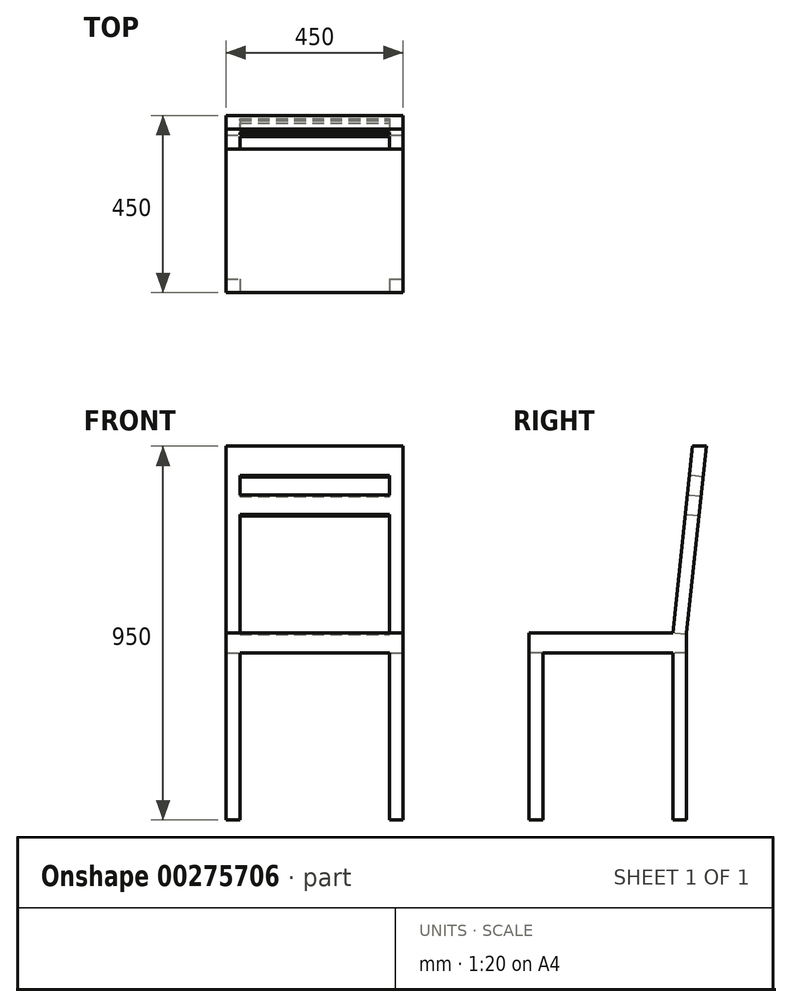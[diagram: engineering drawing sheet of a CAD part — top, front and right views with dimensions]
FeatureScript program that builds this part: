
annotation { "Feature Type Name" : "Feature", "Feature Type Description" : "" }
export const myFeature = defineFeature(function(context is Context, id is Id, definition is map)
    precondition{}
    {
        {
            var Q0;
            Q0=qCreatedBy(makeId("Top.planeOp"),FACE);
            var sketch = newSketch(context, id + "F0", { "sketchPlane" : qUnion([Q0])});
            skLineSegment(sketch, "E0.bottom", {"start": v(225, 225) * mm, "end": v(-225, 225) * mm});
            skLineSegment(sketch, "E0.top", {"start": v(225, -225) * mm, "end": v(-225, -225) * mm});
            skLineSegment(sketch, "E0.left", {"start": v(225, 225) * mm, "end": v(225, -225) * mm});
            skLineSegment(sketch, "E0.right", {"start": v(-225, 225) * mm, "end": v(-225, -225) * mm});
            skPoint(sketch, "E0.middle", {"position": v(0, 0) * mm});
            skSolve(sketch);
        }
        {
            var Q0;
            Q0=qSketchRegion(id+"F0",true);
            extrude(context, id + "F1", {"entities" : qUnion([Q0]), "depth" : 950 * mm});
        }
        {
            var Q0;
            Q0=makeQuery(id+"F1.opExtrude","SWEPT_FACE",FACE,{"disambiguationData":[OSD([sQuery(id+"F0.wireOp",EDGE,"E0.left")])]});
            var sketch = newSketch(context, id + "F2", { "sketchPlane" : qUnion([Q0])});
            skLineSegment(sketch, "E1.bottom", {"start": v(225, 475) * mm, "end": v(-225, 475) * mm});
            skLineSegment(sketch, "E1.top", {"start": v(225, 425) * mm, "end": v(-225, 425) * mm});
            skLineSegment(sketch, "E1.left", {"start": v(225, 475) * mm, "end": v(225, 425) * mm});
            skLineSegment(sketch, "E1.right", {"start": v(-225, 475) * mm, "end": v(-225, 425) * mm});
            skLineSegment(sketch, "E2", {"start": v(225, 950) * mm, "end": v(175, 475) * mm});
            skLineSegment(sketch, "E3", {"start": v(190, 950) * mm, "end": v(140, 475) * mm});
            skLineSegment(sketch, "E4", {"start": v(140, 475) * mm, "end": v(140, 0) * mm});
            skLineSegment(sketch, "E5", {"start": v(175, 475) * mm, "end": v(175, 0) * mm});
            skLineSegment(sketch, "E6.bottom", {"start": v(-225, 0) * mm, "end": v(-190, 0) * mm});
            skLineSegment(sketch, "E6.top", {"start": v(-225, 425) * mm, "end": v(-190, 425) * mm});
            skLineSegment(sketch, "E6.left", {"start": v(-225, 0) * mm, "end": v(-225, 425) * mm});
            skLineSegment(sketch, "E6.right", {"start": v(-190, 0) * mm, "end": v(-190, 425) * mm});
            skLineSegment(sketch, "E7", {"start": v(-225, 950) * mm, "end": v(-225, 0) * mm});
            skSolve(sketch);
        }
        {
            var Q0;
            {var subQ0=sQuery(id+"F2.wireOp",EDGE,"E1.left");Q0=makeQuery(id+"F2.imprint","IMPRINT",FACE,{"disambiguationData":[TD([[makeQuery(id+"F2.imprint","IMPRINT",EDGE,{"derivedFrom":subQ0}),-1.0]])]});}
            var Q1;
            {var subQ4=sQuery(id+"F2.wireOp",EDGE,"E3");Q1=makeQuery(id+"F2.imprint","IMPRINT",FACE,{"disambiguationData":[TD([[makeQuery(id+"F2.imprint","IMPRINT",EDGE,{"derivedFrom":subQ4}),-1.0]])]});}
            var Q2;
            {var subQ4=sQuery(id+"F2.wireOp",EDGE,"E2");Q2=makeQuery(id+"F2.imprint","IMPRINT",FACE,{"disambiguationData":[TD([[makeQuery(id+"F2.imprint","IMPRINT",EDGE,{"derivedFrom":subQ4}),1.0]])]});}
            var Q3;
            {var subQ1=sQuery(id+"F0.wireOp",EDGE,"E0.left");var subQ4=sQuery(id+"F2.wireOp",EDGE,"E5");var subQ6=makeQuery(id+"F1.opExtrude","CAP_EDGE",EDGE,{"disambiguationData":[OSD([subQ1])],"isStart":true});var subQ7=makeQuery(id+"F2.imprint","INTERSECT",VERTEX,{"derivedFrom":[subQ6,subQ4]});Q3=makeQuery(id+"F2.imprint","IMPRINT",FACE,{"disambiguationData":[TD([[makeQuery(id+"F2.imprint","IMPRINT",EDGE,{"disambiguationData":[TD([[subQ7,1.0]])],"derivedFrom":subQ4}),1.0]])]});}
            var Q4;
            {var subQ0=sQuery(id+"F2.wireOp",EDGE,"E6.right");Q4=makeQuery(id+"F2.imprint","IMPRINT",FACE,{"disambiguationData":[TD([[makeQuery(id+"F2.imprint","IMPRINT",EDGE,{"derivedFrom":subQ0}),-1.0]])]});}
            extrude(context, id + "F3", {"entities" : qUnion([Q0, Q1, Q2, Q3, Q4]), "operationType" : NewBodyOperationType.REMOVE, "endBound" : BoundingType.THROUGH_ALL, "oppositeDirection" : true, "depth" : 25 * mm});
        }
        {
            var Q0;
            Q0=makeQuery(id+"F1.opExtrude","SWEPT_FACE",FACE,{"disambiguationData":[OSD([sQuery(id+"F0.wireOp",EDGE,"E0.top")])]});
            var sketch = newSketch(context, id + "F4", { "sketchPlane" : qUnion([Q0])});
            skLineSegment(sketch, "E8", {"start": v(-190, 0) * mm, "end": v(-190, 425) * mm});
            skLineSegment(sketch, "E9", {"start": v(-190, 425) * mm, "end": v(190, 425) * mm});
            skLineSegment(sketch, "E10", {"start": v(190, 425) * mm, "end": v(190, 0) * mm});
            skSolve(sketch);
        }
        {
            var Q0;
            {var subQ0=sQuery(id+"F4.wireOp",EDGE,"E8");Q0=makeQuery(id+"F4.imprint","IMPRINT",FACE,{"disambiguationData":[TD([[makeQuery(id+"F4.imprint","IMPRINT",EDGE,{"derivedFrom":subQ0}),-1.0]])]});}
            extrude(context, id + "F5", {"entities" : qUnion([Q0]), "operationType" : NewBodyOperationType.REMOVE, "endBound" : BoundingType.THROUGH_ALL, "oppositeDirection" : true, "depth" : 25 * mm});
        }
        {
            var Q0;
            Q0=makeQuery(id+"F3.boolean.opBoolean","COPY",FACE,{"derivedFrom":makeQuery(id+"F3.opExtrude","SWEPT_FACE",FACE,{"disambiguationData":[OSD([sQuery(id+"F2.wireOp",EDGE,"E3")])]})});
            var sketch = newSketch(context, id + "F6", { "sketchPlane" : qUnion([Q0])});
            skLineSegment(sketch, "E11", {"start": v(-190, 487.05) * mm, "end": v(-190, 889.67) * mm});
            skLineSegment(sketch, "E12", {"start": v(-190, 889.67) * mm, "end": v(190, 889.67) * mm});
            skLineSegment(sketch, "E13", {"start": v(190, 889.67) * mm, "end": v(190, 487.05) * mm});
            skLineSegment(sketch, "E14", {"start": v(-190, 839.67) * mm, "end": v(190, 839.67) * mm});
            skLineSegment(sketch, "E15", {"start": v(-190, 789.67) * mm, "end": v(190, 789.67) * mm});
            skPoint(sketch, "E15.endSnap0", {"position": v(190, 688.36) * mm});
            skSolve(sketch);
        }
        {
            var Q0;
            {var subQ0=sQuery(id+"F6.wireOp",EDGE,"E12");Q0=makeQuery(id+"F6.imprint","IMPRINT",FACE,{"disambiguationData":[TD([[makeQuery(id+"F6.imprint","IMPRINT",EDGE,{"derivedFrom":subQ0}),-1.0]])]});}
            var Q1;
            {var subQ3=sQuery(id+"F6.wireOp",EDGE,"E15");Q1=makeQuery(id+"F6.imprint","IMPRINT",FACE,{"disambiguationData":[TD([[makeQuery(id+"F6.imprint","IMPRINT",EDGE,{"derivedFrom":subQ3}),-1.0]])]});}
            extrude(context, id + "F7", {"entities" : qUnion([Q0, Q1]), "operationType" : NewBodyOperationType.REMOVE, "endBound" : BoundingType.THROUGH_ALL, "oppositeDirection" : true, "depth" : 25 * mm});
        }
    });
